# Revit family: BOX BSTB LG270
name_source: partatom
category: Modelos genéricos
revit_build: Autodesk Revit 2017 (Build: 20160225_1515(x64)
units: mm (PartAtom-declared; Revit-internal decimal feet)

## family parameters
Compartido = No
Corte con vacíos al cargar = No
Cota de conector redondo = Diámetro de uso
Puede alojar armadura = No
Punto de cálculo de habitación = No
Se basa en plano de trabajo = No
Siempre vertical = Sí
Tipo de pieza = Normal

## types (7) — shared parameters
DIAM = 20 mm
EspPeu = 3 mm  [stored 0.00984252 ft]
P = 41 mm
Q = 60 mm  [stored 0.19685 ft]
URL = www.casals.com
esp = 2 mm  [stored 0.00656168 ft]

## per-type parameters (varying)
| type | A | B | C | Fabricante | J1 | J2 | L | M | N | O | R | Rint | S | T | U | V | VisiblePeuMig | Wint |
| BOX BSTB 355 | 1068 mm | 824 mm | 612 mm | Casals ventilación | 100 mm  [stored 0.328084 ft] | 160 mm  [stored 0.524934 ft] | 965 mm | 809 mm | 101 mm  [stored 0.331365 ft] | 268 mm | 353 mm  [stored 1.15814 ft] | 350 mm  [stored 1.14829 ft] | 307 mm  [stored 1.00722 ft] | 493 mm | 60 mm  [stored 0.19685 ft] | 452 mm | No | 253 mm  [stored 0.830052 ft] |
| BOX BSTB 400 | 1223 mm | 913 mm | 642 mm | Casals Ventilación | 100 mm  [stored 0.328084 ft] | 160 mm  [stored 0.524934 ft] | 1120 mm | 840 mm | 100 mm  [stored 0.328084 ft] | 304 mm  [stored 0.997375 ft] | 398 mm  [stored 1.30577 ft] | 395 mm  [stored 1.29593 ft] | 329 mm  [stored 1.0794 ft] | 541 mm | 60 mm  [stored 0.19685 ft] | 506 mm | No | 281 mm  [stored 0.921916 ft] |
| BOX BSTB 450 | 1323 mm | 1003 mm | 692 mm | Casals ventilación | 100 mm  [stored 0.328084 ft] | 160 mm  [stored 0.524934 ft] | 1220 mm | 890 mm | 100 mm  [stored 0.328084 ft] | 328 mm  [stored 1.07612 ft] | 448 mm  [stored 1.46982 ft] | 445 mm  [stored 1.45997 ft] | 375 mm  [stored 1.23031 ft] | 596 mm | 60 mm  [stored 0.19685 ft] | 572 mm | No | 310 mm  [stored 1.01706 ft] |
| BOX BSTB 500 | 1423 mm | 1100 mm | 732 mm | Casals ventilación | 100 mm  [stored 0.328084 ft] | 160 mm  [stored 0.524934 ft] | 1320 mm | 930 mm | 104 mm | 355 mm | 498 mm | 495 mm | 399 mm  [stored 1.30906 ft] | 653 mm | 60 mm  [stored 0.19685 ft] | 638 mm | No | 341 mm |
| BOX BSTB 560 | 1692 mm | 1216 mm | 802 mm | Casals ventilación | 454 mm  [stored 1.4895 ft] | 514 mm | 1578 mm | 999 mm | 111 mm | 388 mm | 558 mm | 555 mm | 437 mm  [stored 1.43373 ft] | 726 mm | 100 mm  [stored 0.328084 ft] | 715 mm | Sí | 383 mm  [stored 1.25656 ft] |
| BOX BSTB 630 | 1822 mm | 1343 mm | 851 mm | Casals ventilación | 451 mm  [stored 1.47966 ft] | 511 mm | 1708 mm | 1049 mm | 110 mm  [stored 0.360892 ft] | 430 mm | 628 mm | 625 mm | 481 mm  [stored 1.57808 ft] | 803 mm | 100 mm  [stored 0.328084 ft] | 800 mm | Sí | 426 mm  [stored 1.39764 ft] |
| BOX BSTB 710 | 1988 mm | 1488 mm | 912 mm | Casals ventilación | 496 mm | 556 mm | 1875 mm | 1109 mm | 111 mm | 476 mm | 708 mm | 705 mm | 548 mm | 891 mm | 100 mm  [stored 0.328084 ft] | 898 mm | Sí | 479 mm  [stored 1.57152 ft] |

note: [stored X ft] marks values corroborated as IEEE doubles in the binary element streams (Revit-internal decimal feet)
